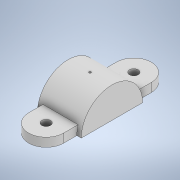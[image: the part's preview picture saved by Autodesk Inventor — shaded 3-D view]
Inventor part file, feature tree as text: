
AUTODESK INVENTOR PART (.ipt)
format: ipt  version: 2020 (Build 240168000, 168)  size: 140,800 bytes
history: native  units: in
note: dims shown in document units (in); Inventor stores cm internally (conversion verified against a paired STEP export)
features: extrude x5, sketch x5
ambient origin geometry x8: Origin, YZ Plane, XZ Plane, XY Plane, X Axis, Y Axis, Z Axis, Center Point
bodies: Solid1 (feature_tree)
feature tree (10):
  extrude  "Extrusion1"  Depth=1.0in
  extrude  "Extrusion2"  Depth=0.5in TaperAngle=0.0deg
  extrude  "rectCut"  Depth=2.5in TaperAngle=0.0deg
  extrude  ".125Hole"  Depth=0.75in
  extrude  "circCut"  Depth=0.125in
  sketch  "Sketch1"  dims[d0=5.0in d1=1.0in]
  sketch  "Sketch2"  dims[d2=0.5in d3=0.5in d4=0.0in]
  sketch  "Sketch3"  dims[d5=1.75in d6=2.5in d7=0.0in]
  sketch  "Sketch4"  dims[d8=2.0in d9=0.75in]
  sketch  "Sketch5"  dims[d10=0.0in d11=0.0in d12=0.125in d13=0.0in d14=0.0in d15=1.25in d16=0.0in d17=0.0in]
